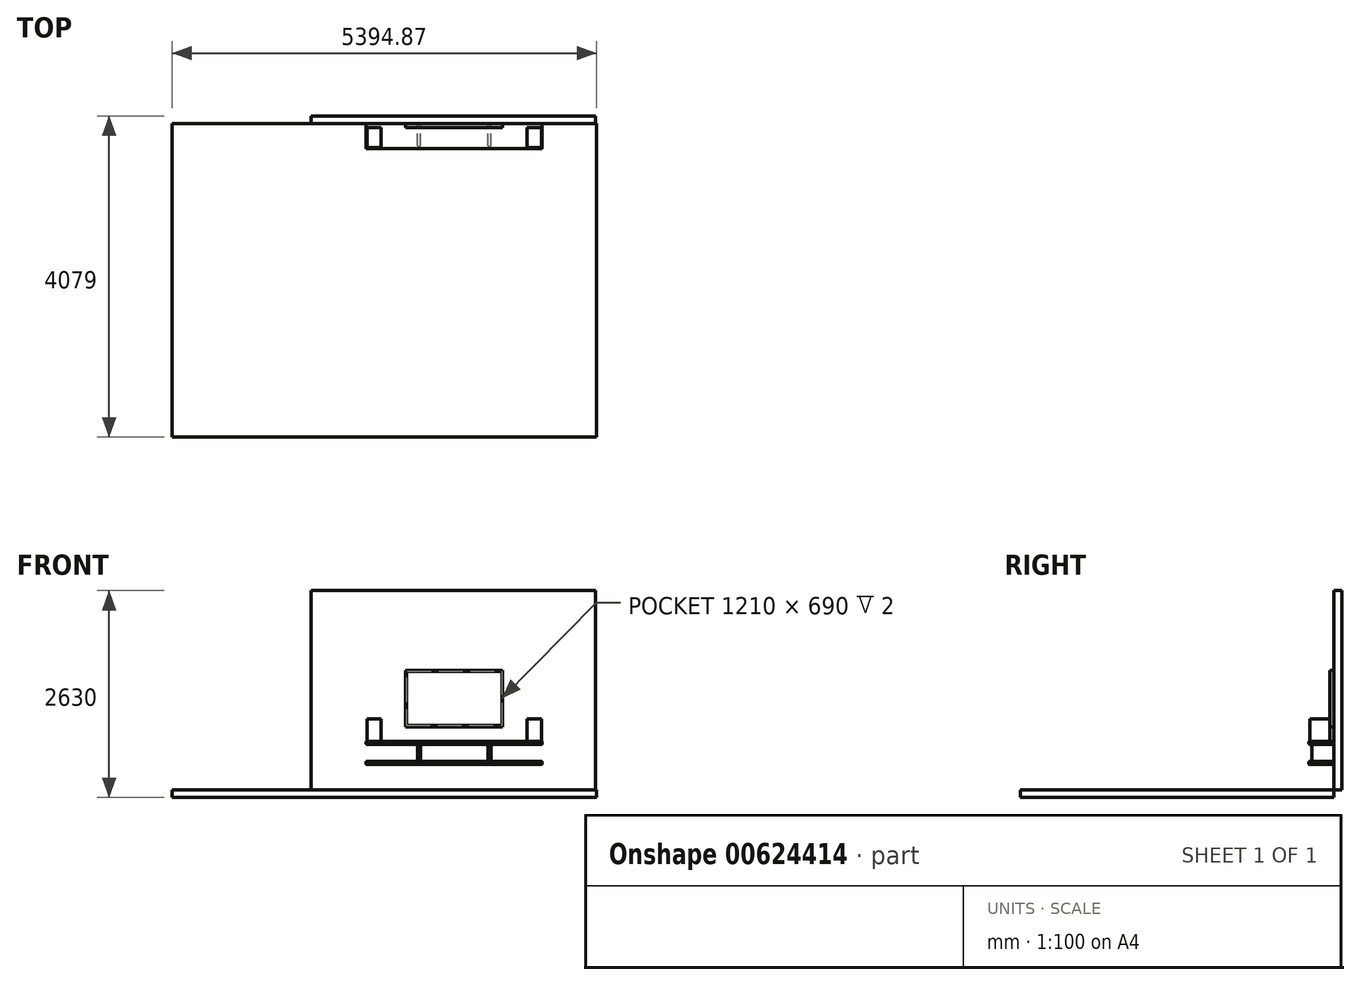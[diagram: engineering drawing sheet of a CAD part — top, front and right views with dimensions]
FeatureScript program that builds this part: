
annotation { "Feature Type Name" : "Feature", "Feature Type Description" : "" }
export const myFeature = defineFeature(function(context is Context, id is Id, definition is map)
    precondition{}
    {
        {
            var Q0;
            Q0=qCreatedBy(makeId("Front.planeOp"),FACE);
            var sketch = newSketch(context, id + "F0", { "sketchPlane" : qUnion([Q0])});
            skLineSegment(sketch, "E0.bottom", {"start": v(-1805, 0) * mm, "end": v(1805, 0) * mm});
            skLineSegment(sketch, "E0.top", {"start": v(-1805, 2530) * mm, "end": v(1805, 2530) * mm});
            skLineSegment(sketch, "E0.left", {"start": v(-1805, 0) * mm, "end": v(-1805, 2530) * mm});
            skLineSegment(sketch, "E0.right", {"start": v(1805, 0) * mm, "end": v(1805, 2530) * mm});
            skPoint(sketch, "E1", {"position": v(0, 0) * mm});
            skSolve(sketch);
        }
        {
            var Q0;
            Q0=makeQuery(id+"F0.imprint","IMPRINT",FACE,{"disambiguationData":[TD([[makeQuery(id+"F0.imprint","IMPRINT",EDGE,{"derivedFrom":sQuery(id+"F0.wireOp",EDGE,"E0.bottom")}),1.0]])]});
            extrude(context, id + "F1", {"entities" : qUnion([Q0]), "oppositeDirection" : true, "depth" : 100 * mm, "offsetDistance" : 25 * mm});
        }
        {
            var Q0;
            Q0=qCreatedBy(makeId("Top.planeOp"),FACE);
            var sketch = newSketch(context, id + "F2", { "sketchPlane" : qUnion([Q0])});
            skLineSegment(sketch, "E2.bottom", {"start": v(1820.18, 0) * mm, "end": v(-3574.69, 0) * mm});
            skLineSegment(sketch, "E2.top", {"start": v(1820.18, -3979) * mm, "end": v(-3574.69, -3979) * mm});
            skLineSegment(sketch, "E2.left", {"start": v(1820.18, 0) * mm, "end": v(1820.18, -3979) * mm});
            skLineSegment(sketch, "E2.right", {"start": v(-3574.69, 0) * mm, "end": v(-3574.69, -3979) * mm});
            skSolve(sketch);
        }
        {
            var Q0;
            Q0=qSketchRegion(id+"F2",true);
            extrude(context, id + "F3", {"entities" : qUnion([Q0]), "operationType" : NewBodyOperationType.ADD, "oppositeDirection" : true, "depth" : 100 * mm, "offsetDistance" : 25 * mm});
        }
        {
            var Q0;
            Q0=makeQuery(id+"F1.opExtrude","CAP_FACE",FACE,{"disambiguationData":[OSD([sQuery(id+"F0.wireOp",EDGE,"E0.bottom"),sQuery(id+"F0.wireOp",EDGE,"E0.top"),sQuery(id+"F0.wireOp",EDGE,"E0.left"),sQuery(id+"F0.wireOp",EDGE,"E0.right")])],"isStart":true});
            var sketch = newSketch(context, id + "F4", { "sketchPlane" : qUnion([Q0])});
            skLineSegment(sketch, "E3.bottom", {"start": v(625, 800) * mm, "end": v(-605, 800) * mm});
            skLineSegment(sketch, "E3.top", {"start": v(625, 1515) * mm, "end": v(-605, 1515) * mm});
            skLineSegment(sketch, "E3.left", {"start": v(625, 800) * mm, "end": v(625, 1515) * mm});
            skLineSegment(sketch, "E3.right", {"start": v(-605, 800) * mm, "end": v(-605, 1515) * mm});
            skPoint(sketch, "E3.middle", {"position": v(10, 1157.5) * mm});
            skSolve(sketch);
        }
        {
            var Q0;
            Q0=qSketchRegion(id+"F4",true);
            extrude(context, id + "F5", {"entities" : qUnion([Q0]), "depth" : 50 * mm, "offsetDistance" : 25 * mm});
        }
        {
            var Q0;
            Q0=makeQuery(id+"F5.opExtrude","CAP_FACE",FACE,{"disambiguationData":[OSD([sQuery(id+"F4.wireOp",EDGE,"E3.bottom"),sQuery(id+"F4.wireOp",EDGE,"E3.top"),sQuery(id+"F4.wireOp",EDGE,"E3.left"),sQuery(id+"F4.wireOp",EDGE,"E3.right")])],"isStart":false});
            var sketch = newSketch(context, id + "F6", { "sketchPlane" : qUnion([Q0])});
            skLineSegment(sketch, "E4.bottom", {"start": v(-595, 1505) * mm, "end": v(615, 1505) * mm});
            skLineSegment(sketch, "E4.top", {"start": v(-595, 815) * mm, "end": v(615, 815) * mm});
            skLineSegment(sketch, "E4.left", {"start": v(-595, 1505) * mm, "end": v(-595, 815) * mm});
            skLineSegment(sketch, "E4.right", {"start": v(615, 1505) * mm, "end": v(615, 815) * mm});
            skSolve(sketch);
        }
        {
            var Q0;
            Q0=qSketchRegion(id+"F6",true);
            extrude(context, id + "F7", {"entities" : qUnion([Q0]), "operationType" : NewBodyOperationType.REMOVE, "oppositeDirection" : true, "depth" : 2 * mm, "offsetDistance" : 25 * mm});
        }
        {
            var Q0;
            Q0=makeQuery(id+"F1.opExtrude","CAP_FACE",FACE,{"disambiguationData":[OSD([sQuery(id+"F0.wireOp",EDGE,"E0.bottom"),sQuery(id+"F0.wireOp",EDGE,"E0.top"),sQuery(id+"F0.wireOp",EDGE,"E0.left"),sQuery(id+"F0.wireOp",EDGE,"E0.right")])],"isStart":true});
            var sketch = newSketch(context, id + "F8", { "sketchPlane" : qUnion([Q0])});
            skLineSegment(sketch, "E5.bottom", {"start": v(-1107.5, 616) * mm, "end": v(1127.5, 616) * mm});
            skLineSegment(sketch, "E5.top", {"start": v(-1107.5, 578) * mm, "end": v(1127.5, 578) * mm});
            skLineSegment(sketch, "E5.left", {"start": v(-1107.5, 616) * mm, "end": v(-1107.5, 578) * mm});
            skLineSegment(sketch, "E5.right", {"start": v(1127.5, 616) * mm, "end": v(1127.5, 578) * mm});
            skLineSegment(sketch, "E6.bottom", {"start": v(-1107.5, 358) * mm, "end": v(1127.5, 358) * mm});
            skLineSegment(sketch, "E6.top", {"start": v(-1107.5, 320) * mm, "end": v(1127.5, 320) * mm});
            skLineSegment(sketch, "E6.left", {"start": v(-1107.5, 358) * mm, "end": v(-1107.5, 320) * mm});
            skLineSegment(sketch, "E6.right", {"start": v(1127.5, 358) * mm, "end": v(1127.5, 320) * mm});
            skPoint(sketch, "E7", {"position": v(10, 616) * mm});
            skPoint(sketch, "E8.0", {"position": v(10, 800) * mm});
            skSolve(sketch);
        }
        {
            var Q0;
            Q0=qSketchRegion(id+"F8",true);
            extrude(context, id + "F9", {"entities" : qUnion([Q0]), "depth" : 315 * mm, "offsetDistance" : 25 * mm});
        }
        {
            var Q0;
            Q0=makeQuery(id+"F1.opExtrude","CAP_FACE",FACE,{"disambiguationData":[OSD([sQuery(id+"F0.wireOp",EDGE,"E0.bottom"),sQuery(id+"F0.wireOp",EDGE,"E0.top"),sQuery(id+"F0.wireOp",EDGE,"E0.left"),sQuery(id+"F0.wireOp",EDGE,"E0.right")])],"isStart":true});
            var sketch = newSketch(context, id + "F10", { "sketchPlane" : qUnion([Q0])});
            skLineSegment(sketch, "E9.bottom", {"start": v(-1107.5, 358) * mm, "end": v(-1069.5, 358) * mm, "construction": true});
            skLineSegment(sketch, "E9.top", {"start": v(-1107.5, 578) * mm, "end": v(-1069.5, 578) * mm, "construction": true});
            skLineSegment(sketch, "E9.left", {"start": v(-1107.5, 358) * mm, "end": v(-1107.5, 578) * mm, "construction": true});
            skLineSegment(sketch, "E9.right", {"start": v(-1069.5, 358) * mm, "end": v(-1069.5, 578) * mm, "construction": true});
            skLineSegment(sketch, "E10.bottom", {"start": v(1089.5, 358) * mm, "end": v(1127.5, 358) * mm, "construction": true});
            skLineSegment(sketch, "E10.top", {"start": v(1089.5, 578) * mm, "end": v(1127.5, 578) * mm, "construction": true});
            skLineSegment(sketch, "E10.left", {"start": v(1089.5, 358) * mm, "end": v(1089.5, 578) * mm, "construction": true});
            skLineSegment(sketch, "E10.right", {"start": v(1127.5, 358) * mm, "end": v(1127.5, 578) * mm, "construction": true});
            skLineSegment(sketch, "E11.bottom", {"start": v(-457.5, 358) * mm, "end": v(-419.5, 358) * mm});
            skLineSegment(sketch, "E11.top", {"start": v(-457.5, 578) * mm, "end": v(-419.5, 578) * mm});
            skLineSegment(sketch, "E11.left", {"start": v(-457.5, 358) * mm, "end": v(-457.5, 578) * mm});
            skLineSegment(sketch, "E11.right", {"start": v(-419.5, 358) * mm, "end": v(-419.5, 578) * mm});
            skLineSegment(sketch, "E12.bottom", {"start": v(439.5, 578) * mm, "end": v(477.5, 578) * mm});
            skLineSegment(sketch, "E12.top", {"start": v(439.5, 358) * mm, "end": v(477.5, 358) * mm});
            skLineSegment(sketch, "E12.left", {"start": v(439.5, 578) * mm, "end": v(439.5, 358) * mm});
            skLineSegment(sketch, "E12.right", {"start": v(477.5, 578) * mm, "end": v(477.5, 358) * mm});
            skSolve(sketch);
        }
        {
            var Q0;
            Q0=qSketchRegion(id+"F10",true);
            extrude(context, id + "F11", {"entities" : qUnion([Q0]), "depth" : 280 * mm, "offsetDistance" : 25 * mm});
        }
        {
            var Q0;
            Q0=makeQuery(id+"F9.opExtrude","CAP_EDGE",EDGE,{"disambiguationData":[OSD([sQuery(id+"F8.wireOp",EDGE,"E5.left")])],"isStart":false});
            var Q1;
            Q1=makeQuery(id+"F9.opExtrude","SWEPT_EDGE",EDGE,{"disambiguationData":[OSD([sQuery(id+"F8.wireOp",EDGE,"E5.bottom"),sQuery(id+"F8.wireOp",EDGE,"E5.left")])]});
            var Q2;
            Q2=makeQuery(id+"F9.opExtrude","SWEPT_EDGE",EDGE,{"disambiguationData":[OSD([sQuery(id+"F8.wireOp",EDGE,"E5.top"),sQuery(id+"F8.wireOp",EDGE,"E5.left")])]});
            var Q3;
            Q3=makeQuery(id+"F9.opExtrude","CAP_EDGE",EDGE,{"disambiguationData":[OSD([sQuery(id+"F8.wireOp",EDGE,"E5.top")])],"isStart":false});
            var Q4;
            Q4=makeQuery(id+"F9.opExtrude","CAP_EDGE",EDGE,{"disambiguationData":[OSD([sQuery(id+"F8.wireOp",EDGE,"E5.bottom")])],"isStart":false});
            var Q5;
            Q5=makeQuery(id+"F9.opExtrude","SWEPT_EDGE",EDGE,{"disambiguationData":[OSD([sQuery(id+"F8.wireOp",EDGE,"E6.bottom"),sQuery(id+"F8.wireOp",EDGE,"E6.left")])]});
            var Q6;
            Q6=makeQuery(id+"F9.opExtrude","SWEPT_EDGE",EDGE,{"disambiguationData":[OSD([sQuery(id+"F8.wireOp",EDGE,"E6.top"),sQuery(id+"F8.wireOp",EDGE,"E6.left")])]});
            var Q7;
            Q7=makeQuery(id+"F9.opExtrude","CAP_EDGE",EDGE,{"disambiguationData":[OSD([sQuery(id+"F8.wireOp",EDGE,"E6.left")])],"isStart":false});
            var Q8;
            Q8=makeQuery(id+"F9.opExtrude","CAP_EDGE",EDGE,{"disambiguationData":[OSD([sQuery(id+"F8.wireOp",EDGE,"E6.top")])],"isStart":false});
            var Q9;
            Q9=makeQuery(id+"F9.opExtrude","SWEPT_EDGE",EDGE,{"disambiguationData":[OSD([sQuery(id+"F8.wireOp",EDGE,"E5.bottom"),sQuery(id+"F8.wireOp",EDGE,"E5.right")])]});
            var Q10;
            Q10=makeQuery(id+"F9.opExtrude","CAP_EDGE",EDGE,{"disambiguationData":[OSD([sQuery(id+"F8.wireOp",EDGE,"E6.right")])],"isStart":false});
            var Q11;
            Q11=makeQuery(id+"F9.opExtrude","SWEPT_EDGE",EDGE,{"disambiguationData":[OSD([sQuery(id+"F8.wireOp",EDGE,"E6.top"),sQuery(id+"F8.wireOp",EDGE,"E6.right")])]});
            var Q12;
            Q12=makeQuery(id+"F9.opExtrude","SWEPT_EDGE",EDGE,{"disambiguationData":[OSD([sQuery(id+"F8.wireOp",EDGE,"E6.bottom"),sQuery(id+"F8.wireOp",EDGE,"E6.right")])]});
            var Q13;
            Q13=makeQuery(id+"F9.opExtrude","SWEPT_EDGE",EDGE,{"disambiguationData":[OSD([sQuery(id+"F8.wireOp",EDGE,"E5.top"),sQuery(id+"F8.wireOp",EDGE,"E5.right")])]});
            var Q14;
            Q14=makeQuery(id+"F9.opExtrude","CAP_EDGE",EDGE,{"disambiguationData":[OSD([sQuery(id+"F8.wireOp",EDGE,"E5.right")])],"isStart":false});
            var Q15;
            Q15=makeQuery(id+"F9.opExtrude","CAP_EDGE",EDGE,{"disambiguationData":[OSD([sQuery(id+"F8.wireOp",EDGE,"E6.bottom")])],"isStart":false});
            fillet(context, id + "F12", {"entities" : qUnion([Q0, Q1, Q2, Q3, Q4, Q5, Q6, Q7, Q8, Q9, Q10, Q11, Q12, Q13, Q14, Q15]), "radius" : 5 * mm, "tangentPropagation" : true, "allowEdgeOverflow" : false});
        }
        {
            var Q0;
            Q0=makeQuery(id+"F11.opExtrude","CAP_EDGE",EDGE,{"disambiguationData":[OSD([sQuery(id+"F10.wireOp",EDGE,"E9.left")])],"isStart":false});
            var Q1;
            Q1=makeQuery(id+"F11.opExtrude","CAP_EDGE",EDGE,{"disambiguationData":[OSD([sQuery(id+"F10.wireOp",EDGE,"E11.left")])],"isStart":false});
            var Q2;
            Q2=makeQuery(id+"F11.opExtrude","CAP_EDGE",EDGE,{"disambiguationData":[OSD([sQuery(id+"F10.wireOp",EDGE,"E10.left")])],"isStart":false});
            var Q3;
            Q3=makeQuery(id+"F11.opExtrude","CAP_EDGE",EDGE,{"disambiguationData":[OSD([sQuery(id+"F10.wireOp",EDGE,"E9.right")])],"isStart":false});
            var Q4;
            Q4=makeQuery(id+"F11.opExtrude","CAP_EDGE",EDGE,{"disambiguationData":[OSD([sQuery(id+"F10.wireOp",EDGE,"E11.right")])],"isStart":false});
            var Q5;
            Q5=makeQuery(id+"F11.opExtrude","CAP_EDGE",EDGE,{"disambiguationData":[OSD([sQuery(id+"F10.wireOp",EDGE,"E10.right")])],"isStart":false});
            var Q6;
            Q6=makeQuery(id+"F11.opExtrude","CAP_EDGE",EDGE,{"disambiguationData":[OSD([sQuery(id+"F10.wireOp",EDGE,"E12.left")])],"isStart":false});
            var Q7;
            Q7=makeQuery(id+"F11.opExtrude","CAP_EDGE",EDGE,{"disambiguationData":[OSD([sQuery(id+"F10.wireOp",EDGE,"E12.right")])],"isStart":false});
            fillet(context, id + "F13", {"entities" : qUnion([Q0, Q1, Q2, Q3, Q4, Q5, Q6, Q7]), "radius" : 5 * mm, "tangentPropagation" : true, "allowEdgeOverflow" : false});
        }
        {
            var Q0;
            Q0=makeQuery(id+"F9.opExtrude","SWEPT_FACE",FACE,{"disambiguationData":[OSD([sQuery(id+"F8.wireOp",EDGE,"E5.bottom")])]});
            var sketch = newSketch(context, id + "F14", { "sketchPlane" : qUnion([Q0])});
            skLineSegment(sketch, "E13.bottom", {"start": v(-1097.5, -300) * mm, "end": v(-917.5, -300) * mm});
            skLineSegment(sketch, "E13.top", {"start": v(-1097.5, -50) * mm, "end": v(-917.5, -50) * mm});
            skLineSegment(sketch, "E13.left", {"start": v(-1097.5, -300) * mm, "end": v(-1097.5, -50) * mm});
            skLineSegment(sketch, "E13.right", {"start": v(-917.5, -300) * mm, "end": v(-917.5, -50) * mm});
            skLineSegment(sketch, "E14.bottom", {"start": v(937.5, -300) * mm, "end": v(1117.5, -300) * mm});
            skLineSegment(sketch, "E14.top", {"start": v(937.5, -50) * mm, "end": v(1117.5, -50) * mm});
            skLineSegment(sketch, "E14.left", {"start": v(937.5, -300) * mm, "end": v(937.5, -50) * mm});
            skLineSegment(sketch, "E14.right", {"start": v(1117.5, -300) * mm, "end": v(1117.5, -50) * mm});
            skSolve(sketch);
        }
        {
            var Q0;
            Q0 = qSketchRegion(id + "F14", true);
            extrude(context, id + "F15", {"entities" : qUnion([Q0]), "depth" : 280 * mm, "offsetDistance" : 25 * mm});
        }
    });
